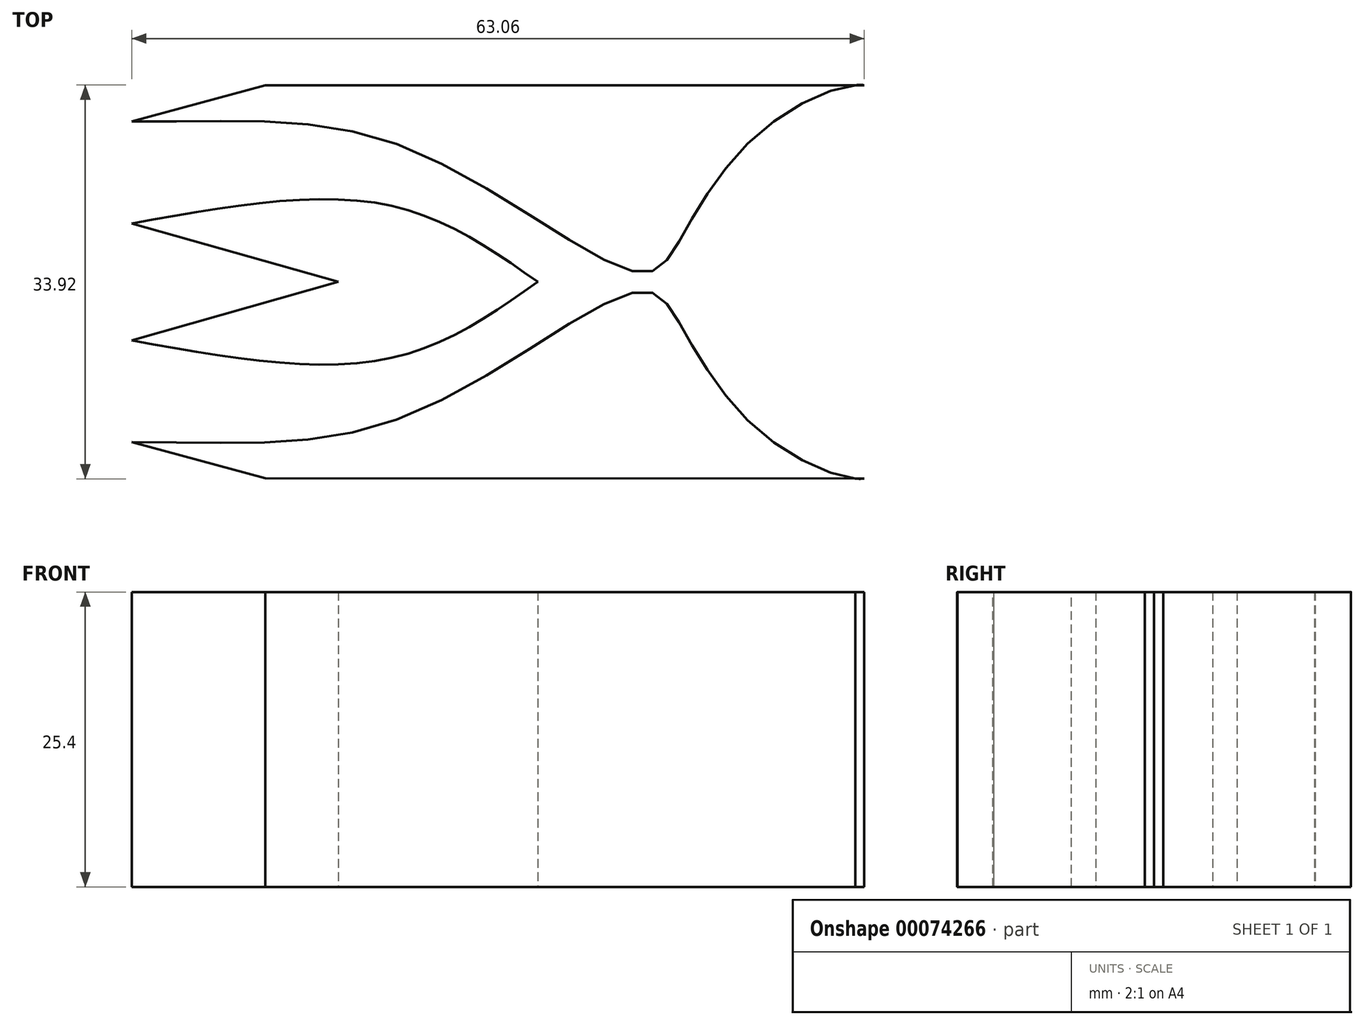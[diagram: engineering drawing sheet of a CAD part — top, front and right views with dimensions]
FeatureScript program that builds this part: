
annotation { "Feature Type Name" : "Feature", "Feature Type Description" : "" }
export const myFeature = defineFeature(function(context is Context, id is Id, definition is map)
    precondition{}
    {
        {
            var Q0;
            Q0=qCreatedBy(makeId("Top.planeOp"),FACE);
            var sketch = newSketch(context, id + "F0", { "sketchPlane" : qUnion([Q0])});
            skFitSpline(sketch, "E0", {"points": [v(-46.22, 13.8) * mm, v(-22.33, 11.46) * mm, v(-2.4, 0.8) * mm, v(0.93, 3.55) * mm, v(7.49, 12.56) * mm, v(16.84, 16.94) * mm, v(19.4, 15.38) * mm], "startDerivative": vector(99.64, -1.5) * mm, "endDerivative": vector(22.26, -24.58) * mm});
            skLineSegment(sketch, "E1", {"start": v(-46.22, 13.8) * mm, "end": v(-34.74, 16.92) * mm});
            skLineSegment(sketch, "E2", {"start": v(-34.74, 16.92) * mm, "end": v(16.84, 16.94) * mm});
            skFitSpline(sketch, "E3", {"points": [v(-11.26, 0) * mm, v(-24.32, 6.65) * mm, v(-46.22, 5.03) * mm], "startDerivative": vector(-26.63, 18.77) * mm, "endDerivative": vector(-42.75, -7.8) * mm});
            skFitSpline(sketch, "E4.MirrorCS", {"points": [v(-46.22, -13.8) * mm, v(-22.33, -11.46) * mm, v(-2.4, -0.8) * mm, v(0.93, -3.55) * mm, v(7.49, -12.56) * mm, v(16.84, -16.94) * mm, v(19.4, -15.38) * mm], "startDerivative": vector(99.64, 1.5) * mm, "endDerivative": vector(22.26, 24.58) * mm});
            skLineSegment(sketch, "E5.MirrorCS", {"start": v(-46.22, -13.8) * mm, "end": v(-34.74, -16.92) * mm});
            skLineSegment(sketch, "E6.MirrorCS", {"start": v(-34.74, -16.92) * mm, "end": v(16.84, -16.94) * mm});
            skFitSpline(sketch, "E7.MirrorCS", {"points": [v(-11.26, 0) * mm, v(-24.32, -6.65) * mm, v(-46.22, -5.03) * mm], "startDerivative": vector(-26.63, -18.77) * mm, "endDerivative": vector(-42.75, 7.8) * mm});
            skLineSegment(sketch, "E8", {"start": v(-46.22, 5.03) * mm, "end": v(-28.43, 0) * mm});
            skLineSegment(sketch, "E9", {"start": v(-28.43, 0) * mm, "end": v(-46.22, -5.03) * mm});
            skSolve(sketch);
        }
        {
            var Q0;
            Q0 = qSketchRegion(id + "F0", true);
            extrude(context, id + "F1", {"entities" : qUnion([Q0]), "depth" : 25.4 * mm});
        }
    });
